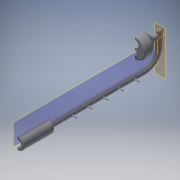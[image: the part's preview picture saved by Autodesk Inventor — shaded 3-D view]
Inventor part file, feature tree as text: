
AUTODESK INVENTOR PART (.ipt)
format: ipt  version: 2018 (Build 220112000, 112)  size: 369,152 bytes
history: native  units: mm
features: sketch x11, extrude x7, projected_geometry x7, fillet x5, plane x3, revolve x2, sweep x1
ambient origin geometry x8: Origin, YZ Plane, XZ Plane, XY Plane, X Axis, Y Axis, Z Axis, Center Point
bodies: Solid1 (feature_tree)
feature tree (36):
  revolve  "Revolution1"  [1 undecoded]
  fillet  "Fillet1"  Radius=40.0mm
  fillet  "Fillet2"  [1 undecoded]
  sweep  "Sweep2"
  plane  "Work Plane6"
  revolve  "Revolution4"  [1 undecoded]
  extrude  "Extrusion10"  Depth=2.0mm
  extrude  "Extrusion11"  Depth=20.0mm TaperAngle=0.0deg
  extrude  "Extrusion15"  Depth=8.25mm
  extrude  "Extrusion4"  Depth=5.0mm
  fillet  "Fillet7"  Radius=1.5mm
  plane  "Work Plane7"
  extrude  "Extrusion12"  Depth=20.0mm
  extrude  "Extrusion13"  TaperAngle=0.0deg  [1 undecoded]
  fillet  "Fillet8"  [1 undecoded]
  plane  "Work Plane8"
  extrude  "Extrusion14"  Depth=9.0mm
  fillet  "Fillet9"  Radius=9.0mm
  sketch  "Sketch1"  dims[d0=160.0mm d3=8.0mm d4=40.0mm d5=90.0deg]
  sketch  "Sketch11"  dims[d20=1.5mm d22=1.5mm]
  sketch  "Sketch17"  dims[d26=1.5mm d27=4.0mm]
  sketch  "Sketch18"  dims[d29=9.0mm d30=2.0mm]
  projected_geometry  "Projected Loop6"
  sketch  "Sketch19"  dims[d31=1.0mm d55=20.0mm d56=0.0mm]
  sketch  "Sketch20"  dims[d73=8.25mm d74=8.25mm]
  projected_geometry  "Projected Loop7"
  sketch  "Sketch21"  dims[d75=0.0mm d78=5.0mm d79=1.5mm]
  projected_geometry  "Projected Loop8"
  sketch  "Sketch22"  dims[d80=20.0mm d81=20.0mm]
  projected_geometry  "Projected Loop9"
  sketch  "Sketch23"  dims[d82=15.0mm d83=0.0mm d84=0.0mm d85=-5.0mm]
  projected_geometry  "Projected Loop10"
  sketch  "Sketch24"  dims[d87=9.822747mm d88=9.0mm d89=9.0mm]
  projected_geometry  "Projected Loop11"
  sketch  "Sketch25"  dims[d90=9.0mm d91=90.0deg d92=2.0mm d93=0.0mm d94=5.0mm d95=5.0mm d96=5.5mm d97=9.0mm d98=2.0mm d99=0.0mm d101=5.0mm d102=4.0mm d103=0.0mm d104=10.0mm d105=0.0mm d106=1.0mm d107=-3.0mm d109=1.5mm d110=14.0mm d111=50.0mm d113=20.0mm d114=10.0mm d116=10.0mm d118=7.0mm d119=0.0mm d120=0.5mm d121=2.0mm d122=1.5mm d123=2.0mm d124=0.0mm d125=2.0mm]
  projected_geometry  "Projected Loop12"
note: 5 required parameter values undecoded (feature->parameter linkage not recoverable at this tier; creation-order binding heuristic only, values carry confidence <= 0.55)